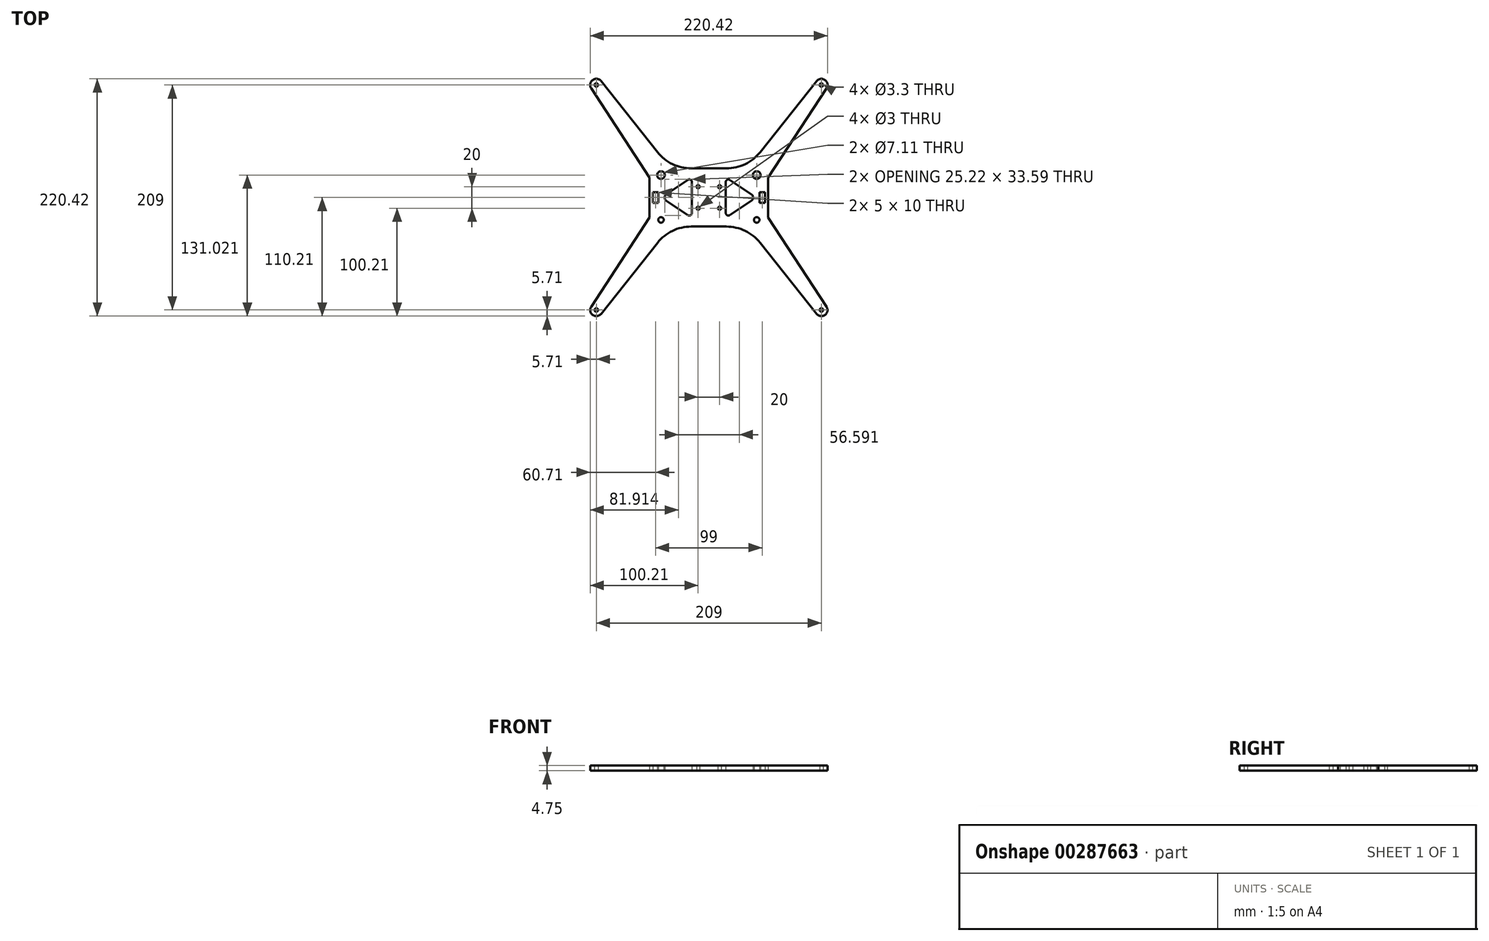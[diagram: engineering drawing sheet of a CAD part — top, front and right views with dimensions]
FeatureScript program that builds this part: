
annotation { "Feature Type Name" : "Feature", "Feature Type Description" : "" }
export const myFeature = defineFeature(function(context is Context, id is Id, definition is map)
    precondition{}
    {
        {
            var Q0;
            Q0=qCreatedBy(makeId("Top.planeOp"),FACE);
            var sketch = newSketch(context, id + "F0", { "sketchPlane" : qUnion([Q0])});
            skLineSegment(sketch, "E0", {"start": v(-39.8, -2.74) * mm, "end": v(-19.58, -16.37) * mm});
            skArc(sketch, "E1", {"start": v(-19.58, -16.37) * mm, "mid": v(-17.01, -16.5) * mm, "end": v(-15.68, -14.3) * mm});
            skLineSegment(sketch, "E2", {"start": v(-15.68, -14.3) * mm, "end": v(-15.68, 14.3) * mm});
            skArc(sketch, "E3", {"start": v(-15.68, 14.3) * mm, "mid": v(-17.01, 16.5) * mm, "end": v(-19.58, 16.37) * mm});
            skLineSegment(sketch, "E4", {"start": v(-19.58, 16.37) * mm, "end": v(-39.8, 2.74) * mm});
            skArc(sketch, "E5", {"start": v(-39.8, 2.74) * mm, "mid": v(-40.61, 1.84) * mm, "end": v(-40.9, 0.67) * mm});
            skLineSegment(sketch, "E6", {"start": v(-40.9, 0.67) * mm, "end": v(-40.9, -0.67) * mm});
            skArc(sketch, "E7", {"start": v(-40.9, -0.67) * mm, "mid": v(-40.61, -1.84) * mm, "end": v(-39.8, -2.74) * mm});
            skLineSegment(sketch, "E8", {"start": v(39.8, 2.74) * mm, "end": v(19.58, 16.37) * mm});
            skArc(sketch, "E9", {"start": v(19.58, 16.37) * mm, "mid": v(17.01, 16.5) * mm, "end": v(15.68, 14.3) * mm});
            skLineSegment(sketch, "E10", {"start": v(15.68, 14.3) * mm, "end": v(15.68, -14.3) * mm});
            skArc(sketch, "E11", {"start": v(15.68, -14.3) * mm, "mid": v(17.01, -16.5) * mm, "end": v(19.58, -16.37) * mm});
            skLineSegment(sketch, "E12", {"start": v(19.58, -16.37) * mm, "end": v(39.8, -2.74) * mm});
            skArc(sketch, "E13", {"start": v(39.8, -2.74) * mm, "mid": v(40.61, -1.84) * mm, "end": v(40.9, -0.67) * mm});
            skLineSegment(sketch, "E14", {"start": v(40.9, -0.67) * mm, "end": v(40.9, 0.67) * mm});
            skArc(sketch, "E15", {"start": v(40.9, 0.67) * mm, "mid": v(40.61, 1.84) * mm, "end": v(39.8, 2.74) * mm});
            skCircle(sketch, "E16", {"center": v(104.5, 104.5) * mm, "radius": 1.65 * mm});
            skCircle(sketch, "E17", {"center": v(44.44, 20.81) * mm, "radius": 3.56 * mm});
            skCircle(sketch, "E18", {"center": v(-104.5, 104.5) * mm, "radius": 1.65 * mm});
            skLineSegment(sketch, "E19", {"start": v(-100.03, 108.05) * mm, "end": v(-47.64, 42.12) * mm});
            skArc(sketch, "E20", {"start": v(-47.64, 42.12) * mm, "mid": v(-33.71, 30.98) * mm, "end": v(-16.32, 27) * mm});
            skLineSegment(sketch, "E21", {"start": v(-16.32, 27) * mm, "end": v(16.32, 27) * mm});
            skArc(sketch, "E22", {"start": v(16.32, 27) * mm, "mid": v(33.71, 30.98) * mm, "end": v(47.64, 42.12) * mm});
            skLineSegment(sketch, "E23", {"start": v(47.64, 42.12) * mm, "end": v(100.03, 108.05) * mm});
            skArc(sketch, "E24", {"start": v(100.03, 108.05) * mm, "mid": v(107.84, 109.12) * mm, "end": v(109.27, 101.37) * mm});
            skLineSegment(sketch, "E25", {"start": v(109.27, 101.37) * mm, "end": v(55, 18.66) * mm});
            skLineSegment(sketch, "E26", {"start": v(55, 18.66) * mm, "end": v(55, -18.66) * mm});
            skLineSegment(sketch, "E27", {"start": v(55, -18.66) * mm, "end": v(109.27, -101.37) * mm});
            skArc(sketch, "E28", {"start": v(109.27, -101.37) * mm, "mid": v(107.84, -109.12) * mm, "end": v(100.03, -108.05) * mm});
            skLineSegment(sketch, "E29", {"start": v(100.03, -108.05) * mm, "end": v(47.64, -42.12) * mm});
            skArc(sketch, "E30", {"start": v(47.64, -42.12) * mm, "mid": v(33.71, -30.98) * mm, "end": v(16.33, -27) * mm});
            skLineSegment(sketch, "E31", {"start": v(16.33, -27) * mm, "end": v(-16.33, -27) * mm});
            skArc(sketch, "E32", {"start": v(-16.33, -27) * mm, "mid": v(-33.71, -30.98) * mm, "end": v(-47.64, -42.12) * mm});
            skLineSegment(sketch, "E33", {"start": v(-47.64, -42.12) * mm, "end": v(-100.03, -108.05) * mm});
            skArc(sketch, "E34", {"start": v(-100.03, -108.05) * mm, "mid": v(-107.84, -109.12) * mm, "end": v(-109.27, -101.37) * mm});
            skLineSegment(sketch, "E35", {"start": v(-109.27, -101.37) * mm, "end": v(-55, -18.66) * mm});
            skLineSegment(sketch, "E36", {"start": v(-55, -18.66) * mm, "end": v(-55, 18.66) * mm});
            skLineSegment(sketch, "E37", {"start": v(-55, 18.66) * mm, "end": v(-109.27, 101.37) * mm});
            skArc(sketch, "E38", {"start": v(-109.27, 101.37) * mm, "mid": v(-107.84, 109.12) * mm, "end": v(-100.03, 108.05) * mm});
            skCircle(sketch, "E39", {"center": v(-44.44, 20.81) * mm, "radius": 3.56 * mm});
            skCircle(sketch, "E40", {"center": v(10, 10) * mm, "radius": 1.5 * mm});
            skCircle(sketch, "E41", {"center": v(-10, -10) * mm, "radius": 1.5 * mm});
            skCircle(sketch, "E42", {"center": v(10, -10) * mm, "radius": 1.5 * mm});
            skCircle(sketch, "E43", {"center": v(-10, 10) * mm, "radius": 1.5 * mm});
            skLineSegment(sketch, "E44", {"start": v(-52, -5) * mm, "end": v(-47, -5) * mm});
            skLineSegment(sketch, "E45", {"start": v(-47, -5) * mm, "end": v(-47, 5) * mm});
            skLineSegment(sketch, "E46", {"start": v(-47, 5) * mm, "end": v(-52, 5) * mm});
            skLineSegment(sketch, "E47", {"start": v(-52, 5) * mm, "end": v(-52, -5) * mm});
            skLineSegment(sketch, "E48", {"start": v(47, 5) * mm, "end": v(47, -5) * mm});
            skLineSegment(sketch, "E49", {"start": v(47, -5) * mm, "end": v(52, -5) * mm});
            skLineSegment(sketch, "E50", {"start": v(52, -5) * mm, "end": v(52, 5) * mm});
            skLineSegment(sketch, "E51", {"start": v(52, 5) * mm, "end": v(47, 5) * mm});
            skCircle(sketch, "E52", {"center": v(-44.44, -20.8) * mm, "radius": 2.55 * mm});
            skCircle(sketch, "E53", {"center": v(-104.5, -104.5) * mm, "radius": 1.65 * mm});
            skCircle(sketch, "E54", {"center": v(44.44, -20.8) * mm, "radius": 2.55 * mm});
            skCircle(sketch, "E55", {"center": v(104.5, -104.5) * mm, "radius": 1.65 * mm});
            skSolve(sketch);
        }
        {
            var Q0;
            Q0=makeQuery(id+"F0.imprint","IMPRINT",FACE,{"disambiguationData":[TD([[makeQuery(id+"F0.imprint","IMPRINT",EDGE,{"derivedFrom":sQuery(id+"F0.wireOp",EDGE,"E0")}),-1.0]])]});
            extrude(context, id + "F1", {"entities" : qUnion([Q0]), "depth" : 4.75 * mm, "offsetDistance" : 25 * mm});
        }
    });
